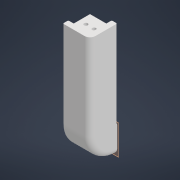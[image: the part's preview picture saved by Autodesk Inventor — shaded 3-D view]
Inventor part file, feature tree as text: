
AUTODESK INVENTOR PART (.ipt)
format: ipt  version: 2021 (Build 250183000, 183)  size: 244,224 bytes
history: native  units: mm
features: sketch x9, extrude x8, other x4, reference x3, projected_geometry x2, plane x1, revolve x1
ambient origin geometry x8: Origin, YZ Plane, XZ Plane, XY Plane, X Axis, Y Axis, Z Axis, Center Point
bodies: Solid1 (feature_tree)
feature tree (28):
  plane  "Work Plane1"
  revolve  "Revolution1"  [1 undecoded]
  sketch  "Sketch2"  dims[d10=5.0mm d11=5.0mm]
  other  "Work Point1"
  extrude  "Extrusion1"  Depth=5.0mm
  extrude  "Extrusion4"  Depth=10.0mm
  extrude  "Extrusion5"  TaperAngle=0.0deg  [1 undecoded]
  extrude  "Extrusion6"  Depth=10.0mm TaperAngle=0.0deg
  extrude  "Extrusion7"  Depth=10.0mm TaperAngle=0.0deg
  extrude  "Extrusion8"  Depth=5.8mm
  extrude  "Extrusion9"  Depth=2.7mm
  extrude  "Extrusion10"  Depth=5.0mm TaperAngle=0.0deg
  sketch  "Sketch1"  dims[d0=90.0deg d1=10.0mm d2=0.0mm]
  reference  "Reference1"
  projected_geometry  "Projected Loop1"
  sketch  "Sketch5"  dims[d12=10.0mm d13=0.0mm d14=7.5mm]
  sketch  "Sketch6"  dims[d15=3.3mm d16=0.0mm d17=0.0mm]
  sketch  "Sketch8"  dims[d18=10.0mm d19=10.0mm d20=0.0mm]
  sketch  "Sketch9"  dims[d21=3.3mm d22=10.0mm d23=0.0mm]
  reference  "Reference3"
  sketch  "Sketch11"  dims[d27=9.600037mm d28=5.8mm]
  sketch  "Sketch12"  dims[d29=2.7mm d30=0.0mm d31=2.7mm]
  projected_geometry  "Projected Loop2"
  sketch  "Sketch13"  dims[d32=2.7mm d33=0.0mm d34=5.0mm d35=0.0mm]
  reference  "Reference4"
  other  "<userpath>\green-house\green-house.iam"
  other  "green-house.iam"
  other  "frame:1"
note: 2 required parameter values undecoded (feature->parameter linkage not recoverable at this tier; creation-order binding heuristic only, values carry confidence <= 0.55)